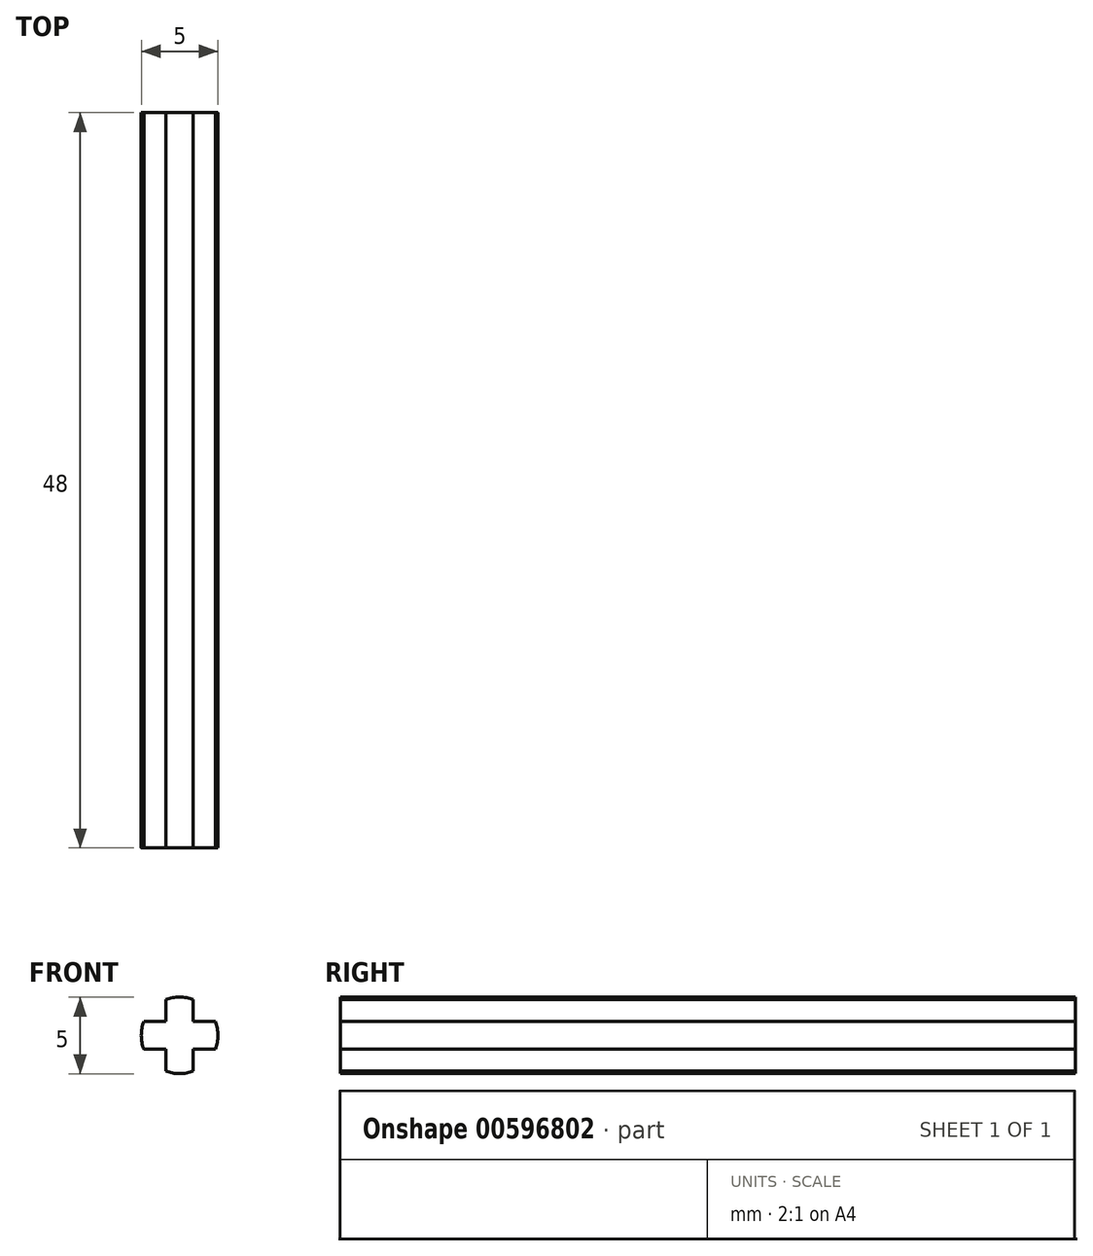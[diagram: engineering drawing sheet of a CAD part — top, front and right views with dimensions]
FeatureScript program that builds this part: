
annotation { "Feature Type Name" : "Feature", "Feature Type Description" : "" }
export const myFeature = defineFeature(function(context is Context, id is Id, definition is map)
    precondition{}
    {
        {
            var Q0;
            Q0=qCreatedBy(makeId("Front.planeOp"),FACE);
            var sketch = newSketch(context, id + "F0", { "sketchPlane" : qUnion([Q0])});
            skArc(sketch, "E0", {"start": v(2.32, -0.88) * mm, "mid": v(2.49, 0.02) * mm, "end": v(2.32, 0.92) * mm});
            skLineSegment(sketch, "E1.left", {"start": v(-0.91, 2.35) * mm, "end": v(-0.91, 0.92) * mm});
            skLineSegment(sketch, "E1.right", {"start": v(0.89, 2.35) * mm, "end": v(0.89, 0.92) * mm});
            skLineSegment(sketch, "E2.bottom", {"start": v(2.32, 0.92) * mm, "end": v(0.89, 0.92) * mm});
            skLineSegment(sketch, "E2.top", {"start": v(2.32, -0.88) * mm, "end": v(0.89, -0.88) * mm});
            skArc(sketch, "E3.trimOffspring", {"start": v(0.89, 2.35) * mm, "mid": v(-0.01, 2.52) * mm, "end": v(-0.91, 2.35) * mm});
            skArc(sketch, "E4.trimOffspring", {"start": v(-2.34, 0.92) * mm, "mid": v(-2.51, 0.02) * mm, "end": v(-2.34, -0.88) * mm});
            skArc(sketch, "E5.trimOffspring", {"start": v(-0.91, -2.3) * mm, "mid": v(-0.01, -2.48) * mm, "end": v(0.89, -2.3) * mm});
            skLineSegment(sketch, "E6.trimOffspring", {"start": v(-0.91, -0.88) * mm, "end": v(-0.91, -2.3) * mm});
            skLineSegment(sketch, "E7.trimOffspring", {"start": v(-0.91, 0.92) * mm, "end": v(-2.34, 0.92) * mm});
            skLineSegment(sketch, "E8.trimOffspring", {"start": v(0.89, -0.88) * mm, "end": v(0.89, -2.3) * mm});
            skLineSegment(sketch, "E9.trimOffspring", {"start": v(-0.91, -0.88) * mm, "end": v(-2.34, -0.88) * mm});
            skSolve(sketch);
        }
        {
            var Q0;
            Q0=qSketchRegion(id+"F0",true);
            extrude(context, id + "F1", {"entities" : qUnion([Q0]), "endBound" : BoundingType.SYMMETRIC, "depth" : 48 * mm, "offsetDistance" : 25 * mm});
        }
    });
